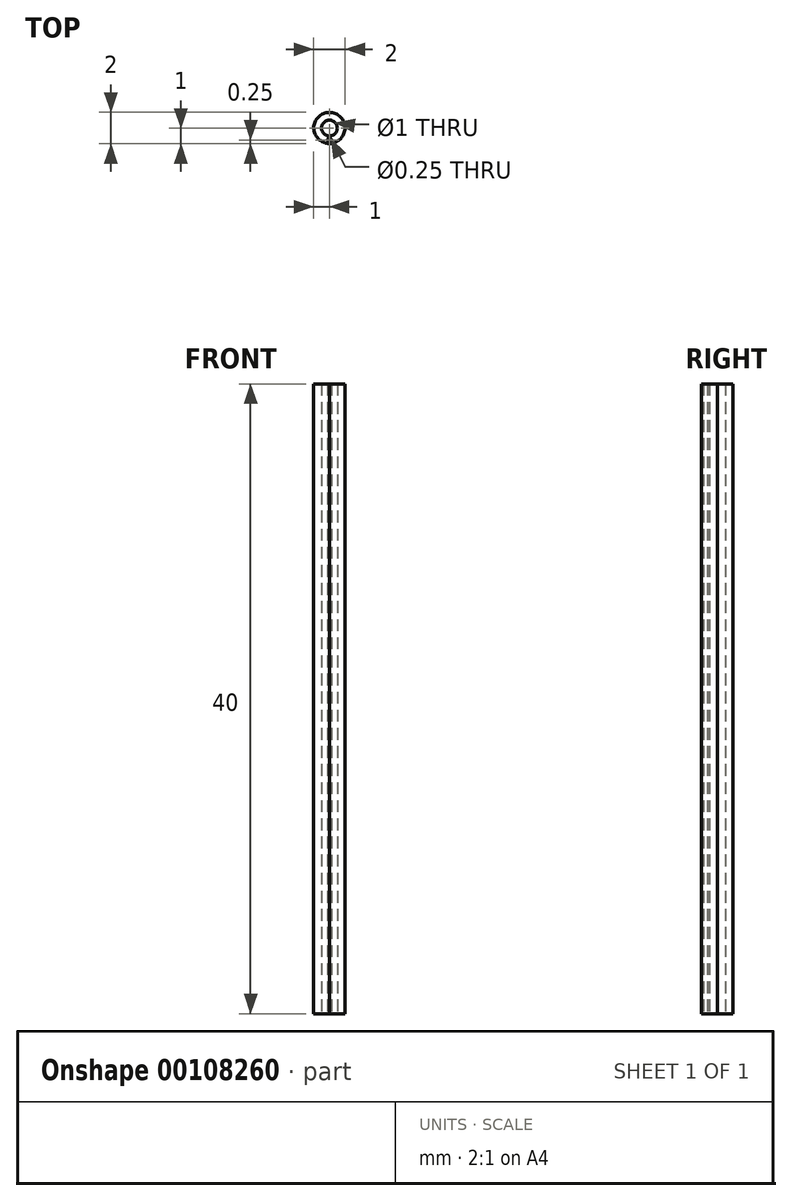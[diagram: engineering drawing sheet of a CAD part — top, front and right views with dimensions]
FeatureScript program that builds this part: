
annotation { "Feature Type Name" : "Feature", "Feature Type Description" : "" }
export const myFeature = defineFeature(function(context is Context, id is Id, definition is map)
    precondition{}
    {
        {
            var Q0;
            Q0=qCreatedBy(makeId("Top.planeOp"),FACE);
            var sketch = newSketch(context, id + "F0", { "sketchPlane" : qUnion([Q0])});
            skCircle(sketch, "E0", {"center": v(0, 0) * mm, "radius": 0.5 * mm});
            skLineSegment(sketch, "E1", {"start": v(-1, 0) * mm, "end": v(1, 0) * mm, "construction": true});
            skLineSegment(sketch, "E2", {"start": v(0, 0) * mm, "end": v(0, 1) * mm, "construction": true});
            skArc(sketch, "E3", {"start": v(1, 0) * mm, "mid": v(0, 1) * mm, "end": v(-1, 0) * mm});
            skCircle(sketch, "E4", {"center": v(0, -0.75) * mm, "radius": 0.12 * mm});
            skLineSegment(sketch, "E5", {"start": v(0, 0) * mm, "end": v(0, -0.75) * mm, "construction": true});
            skLineSegment(sketch, "E6", {"start": v(0, 0) * mm, "end": v(0, -1) * mm, "construction": true});
            skArc(sketch, "E7", {"start": v(0, -1) * mm, "mid": v(0.69, -0.69) * mm, "end": v(1, 0) * mm});
            skArc(sketch, "E8", {"start": v(-1, 0) * mm, "mid": v(-0.69, -0.69) * mm, "end": v(0, -1) * mm});
            skLineSegment(sketch, "E9", {"start": v(0, -0.62) * mm, "end": v(0, -0.5) * mm, "construction": true});
            skLineSegment(sketch, "E10", {"start": v(0, -1) * mm, "end": v(0, -0.88) * mm, "construction": true});
            skSolve(sketch);
        }
        {
            var Q0;
            Q0=makeQuery(id+"F0.imprint","IMPRINT",FACE,{"disambiguationData":[TD([[makeQuery(id+"F0.imprint","IMPRINT",EDGE,{"derivedFrom":sQuery(id+"F0.wireOp",EDGE,"E0")}),-1.0]])]});
            extrude(context, id + "F1", {"entities" : qUnion([Q0]), "depth" : 40 * mm});
        }
    });
